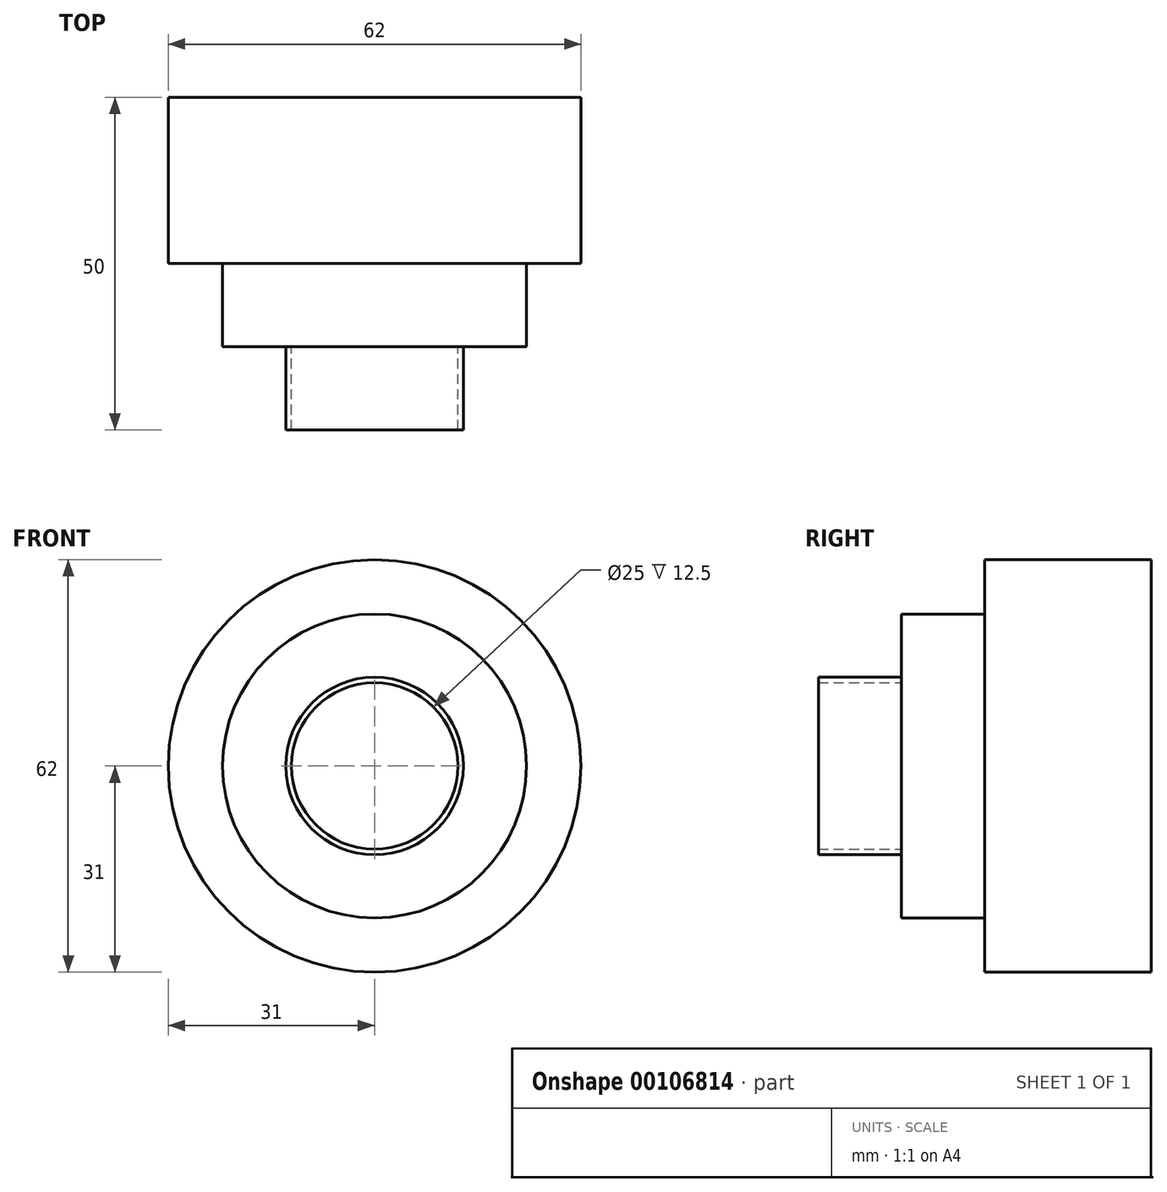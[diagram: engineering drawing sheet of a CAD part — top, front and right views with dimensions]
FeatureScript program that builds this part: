
annotation { "Feature Type Name" : "Feature", "Feature Type Description" : "" }
export const myFeature = defineFeature(function(context is Context, id is Id, definition is map)
    precondition{}
    {
        {
            var Q0;
            Q0=qCreatedBy(makeId("Front.planeOp"),FACE);
            var sketch = newSketch(context, id + "F0", { "sketchPlane" : qUnion([Q0])});
            skCircle(sketch, "E0", {"center": v(0, 0) * mm, "radius": 31 * mm});
            skSolve(sketch);
        }
        {
            var Q0;
            Q0 = qSketchRegion(id + "F0", true);
            extrude(context, id + "F1", {"entities" : qUnion([Q0]), "endBound" : BoundingType.SYMMETRIC, "depth" : 25 * mm});
        }
        {
            var Q0;
            Q0=qCreatedBy(makeId("Front.planeOp"),FACE);
            var sketch = newSketch(context, id + "F2", { "sketchPlane" : qUnion([Q0])});
            skCircle(sketch, "E1", {"center": v(0, 0) * mm, "radius": 22.83 * mm});
            skCircle(sketch, "E2", {"center": v(0, 0) * mm, "radius": 28.01 * mm, "construction": true});
            skCircle(sketch, "E3", {"center": v(0, 0) * mm, "radius": 20.91 * mm, "construction": true});
            skSolve(sketch);
        }
        {
            var Q0;
            Q0 = qSketchRegion(id + "F2", true);
            extrude(context, id + "F3", {"entities" : qUnion([Q0]), "operationType" : NewBodyOperationType.ADD, "depth" : 25 * mm});
        }
        {
            var Q0;
            Q0=makeQuery(id+"F3.opExtrude","CAP_FACE",FACE,{"disambiguationData":[OSD([sQuery(id+"F2.wireOp",EDGE,"E1")])],"isStart":false});
            var sketch = newSketch(context, id + "F4", { "sketchPlane" : qUnion([Q0])});
            skCircle(sketch, "E4", {"center": v(0, 0) * mm, "radius": 13.33 * mm});
            skCircle(sketch, "E5", {"center": v(0, 0) * mm, "radius": 12.5 * mm});
            skCircle(sketch, "E6", {"center": v(0, 0) * mm, "radius": 6 * mm});
            skSolve(sketch);
        }
        {
            var Q0;
            Q0=makeQuery(id+"F4.imprint","IMPRINT",FACE,{"disambiguationData":[TD([[makeQuery(id+"F4.imprint","IMPRINT",EDGE,{"derivedFrom":sQuery(id+"F4.wireOp",EDGE,"E4")}),1.0]])]});
            extrude(context, id + "F5", {"entities" : qUnion([Q0]), "operationType" : NewBodyOperationType.ADD, "endBound" : BoundingType.SYMMETRIC, "depth" : 25 * mm});
        }
    });
